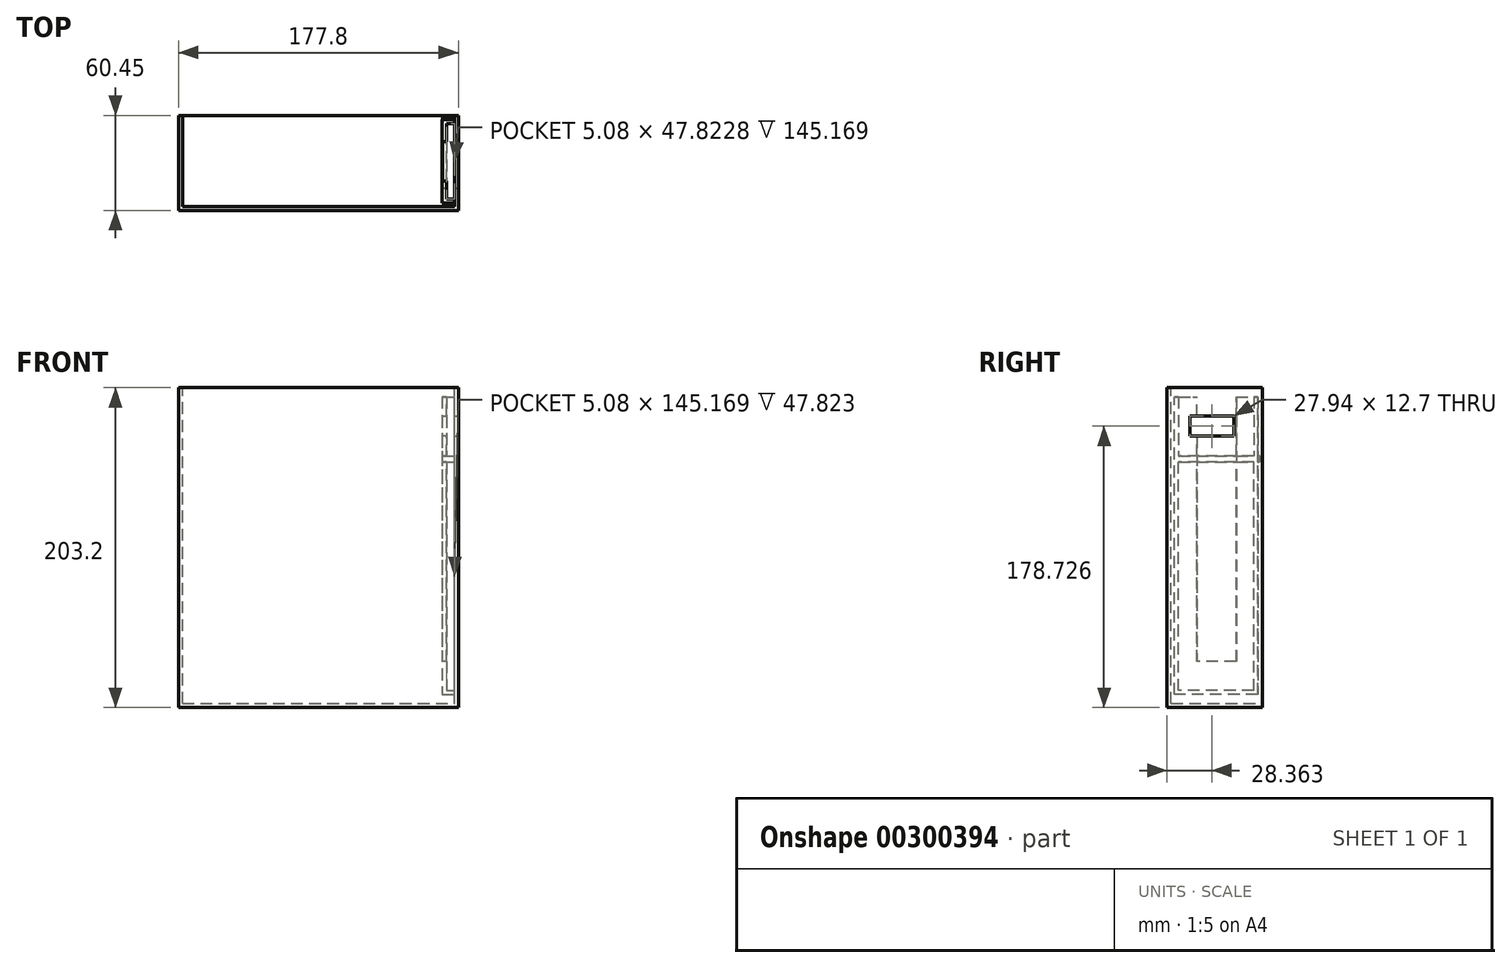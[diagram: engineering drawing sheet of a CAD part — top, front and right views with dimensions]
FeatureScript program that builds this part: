
annotation { "Feature Type Name" : "Feature", "Feature Type Description" : "" }
export const myFeature = defineFeature(function(context is Context, id is Id, definition is map)
    precondition{}
    {
        {
            var Q0;
            Q0=qCreatedBy(makeId("Front.planeOp"),FACE);
            var sketch = newSketch(context, id + "F0", { "sketchPlane" : qUnion([Q0])});
            skLineSegment(sketch, "E0.bottom", {"start": v(-89.23, 0) * mm, "end": v(88.57, 0) * mm});
            skLineSegment(sketch, "E0.top", {"start": v(-89.23, 203.2) * mm, "end": v(88.57, 203.2) * mm});
            skLineSegment(sketch, "E0.left", {"start": v(-89.23, 0) * mm, "end": v(-89.23, 203.2) * mm});
            skLineSegment(sketch, "E0.right", {"start": v(88.57, 0) * mm, "end": v(88.57, 203.2) * mm});
            skSolve(sketch);
        }
        {
            var Q0;
            Q0 = qSketchRegion(id + "F0", true);
            extrude(context, id + "F1", {"entities" : qUnion([Q0]), "depth" : 63.5 * mm});
        }
        {
            var Q0;
            Q0=makeQuery(id+"F1.opExtrude","SWEPT_FACE",FACE,{"disambiguationData":[OSD([sQuery(id+"F0.wireOp",EDGE,"E0.top")])]});
            shell(context, id + "F2", {"entities" : qUnion([Q0]), "thickness" : 2.54 * mm});
        }
        {
            var Q0;
            Q0=makeQuery(id+"F1.opExtrude","SWEPT_FACE",FACE,{"disambiguationData":[OSD([sQuery(id+"F0.wireOp",EDGE,"E0.right")])]});
            var sketch = newSketch(context, id + "F3", { "sketchPlane" : qUnion([Q0])});
            skLineSegment(sketch, "E1.bottom", {"start": v(-58.78, 197.36) * mm, "end": v(-5.88, 197.36) * mm});
            skLineSegment(sketch, "E1.top", {"start": v(-58.78, 8.2) * mm, "end": v(-5.88, 8.2) * mm});
            skLineSegment(sketch, "E1.left", {"start": v(-58.78, 197.36) * mm, "end": v(-58.78, 8.2) * mm});
            skLineSegment(sketch, "E1.right", {"start": v(-5.88, 197.36) * mm, "end": v(-5.88, 8.2) * mm});
            skSolve(sketch);
        }
        {
            var Q0;
            Q0 = qSketchRegion(id + "F3", true);
            extrude(context, id + "F4", {"entities" : qUnion([Q0]), "operationType" : NewBodyOperationType.ADD, "oppositeDirection" : true, "depth" : 10.16 * mm});
        }
        {
            var Q0;
            Q0=makeQuery(id+"F4.opExtrude","SWEPT_FACE",FACE,{"disambiguationData":[OSD([sQuery(id+"F3.wireOp",EDGE,"E1.bottom")])]});
            shell(context, id + "F5", {"entities" : qUnion([Q0]), "thickness" : 2.54 * mm});
        }
        {
            var Q0;
            Q0=makeQuery(id+"F4.opExtrude","CAP_FACE",FACE,{"disambiguationData":[OSD([sQuery(id+"F3.wireOp",EDGE,"E1.bottom"),sQuery(id+"F3.wireOp",EDGE,"E1.top"),sQuery(id+"F3.wireOp",EDGE,"E1.left"),sQuery(id+"F3.wireOp",EDGE,"E1.right")])],"isStart":false});
            var sketch = newSketch(context, id + "F6", { "sketchPlane" : qUnion([Q0])});
            skLineSegment(sketch, "E2.bottom", {"start": v(44.67, 197.36) * mm, "end": v(19.62, 197.36) * mm});
            skLineSegment(sketch, "E2.top", {"start": v(44.67, 8.2) * mm, "end": v(19.62, 8.2) * mm});
            skLineSegment(sketch, "E2.left", {"start": v(44.67, 197.36) * mm, "end": v(44.67, 8.2) * mm});
            skLineSegment(sketch, "E2.right", {"start": v(19.62, 197.36) * mm, "end": v(19.62, 8.2) * mm});
            skLineSegment(sketch, "E3", {"start": v(44.67, 29.18) * mm, "end": v(19.62, 29.18) * mm});
            skSolve(sketch);
        }
        {
            var Q0;
            {var subQ0=sQuery(id+"F6.wireOp",EDGE,"E2.bottom");Q0=makeQuery(id+"F6.imprint","IMPRINT",FACE,{"disambiguationData":[TD([[makeQuery(id+"F6.imprint","IMPRINT",EDGE,{"derivedFrom":subQ0}),1.0]])]});}
            extrude(context, id + "F7", {"entities" : qUnion([Q0]), "operationType" : NewBodyOperationType.REMOVE, "oppositeDirection" : true, "depth" : 5.84 * mm});
        }
        {
            var Q0;
            Q0=makeQuery(id+"F1.opExtrude","SWEPT_FACE",FACE,{"disambiguationData":[OSD([sQuery(id+"F0.wireOp",EDGE,"E0.right")])]});
            var sketch = newSketch(context, id + "F8", { "sketchPlane" : qUnion([Q0])});
            skLineSegment(sketch, "E4.bottom", {"start": v(-49.1, 190.16) * mm, "end": v(-21.17, 190.16) * mm});
            skLineSegment(sketch, "E4.top", {"start": v(-49.1, 159.68) * mm, "end": v(-21.17, 159.68) * mm});
            skLineSegment(sketch, "E4.left", {"start": v(-49.1, 190.16) * mm, "end": v(-49.1, 159.68) * mm});
            skLineSegment(sketch, "E4.right", {"start": v(-21.17, 190.16) * mm, "end": v(-21.17, 159.68) * mm});
            skLineSegment(sketch, "E5", {"start": v(-49.1, 172.38) * mm, "end": v(-21.17, 172.38) * mm});
            skLineSegment(sketch, "E6", {"start": v(-21.17, 185.08) * mm, "end": v(-49.1, 185.08) * mm});
            skSolve(sketch);
        }
        {
            var Q0;
            {var subQ0=sQuery(id+"F8.wireOp",EDGE,"E5");Q0=makeQuery(id+"F8.imprint","IMPRINT",FACE,{"disambiguationData":[TD([[makeQuery(id+"F8.imprint","IMPRINT",EDGE,{"derivedFrom":subQ0}),1.0]])]});}
            extrude(context, id + "F9", {"entities" : qUnion([Q0]), "operationType" : NewBodyOperationType.REMOVE, "oppositeDirection" : true, "depth" : 25.4 * mm});
        }
        {
            var Q0;
            Q0=makeQuery(id+"F1.opExtrude","SWEPT_FACE",FACE,{"disambiguationData":[OSD([sQuery(id+"F0.wireOp",EDGE,"E0.right")])]});
            var sketch = newSketch(context, id + "F10", { "sketchPlane" : qUnion([Q0])});
            skLineSegment(sketch, "E7.bottom", {"start": v(-58.79, 159.68) * mm, "end": v(-4.56, 159.68) * mm});
            skLineSegment(sketch, "E7.top", {"start": v(-58.79, 155.9) * mm, "end": v(-4.56, 155.9) * mm});
            skLineSegment(sketch, "E7.left", {"start": v(-58.79, 159.68) * mm, "end": v(-58.79, 155.9) * mm});
            skLineSegment(sketch, "E7.right", {"start": v(-4.56, 159.68) * mm, "end": v(-4.56, 155.9) * mm});
            skSolve(sketch);
        }
        {
            var Q0;
            Q0 = qSketchRegion(id + "F10", true);
            extrude(context, id + "F11", {"entities" : qUnion([Q0]), "operationType" : NewBodyOperationType.ADD, "oppositeDirection" : true, "depth" : 9.9 * mm});
        }
        {
            var Q0;
            Q0=makeQuery(id+"F1.opExtrude","CAP_FACE",FACE,{"disambiguationData":[OSD([sQuery(id+"F0.wireOp",EDGE,"E0.bottom"),sQuery(id+"F0.wireOp",EDGE,"E0.top"),sQuery(id+"F0.wireOp",EDGE,"E0.left"),sQuery(id+"F0.wireOp",EDGE,"E0.right")])],"isStart":true});
            extrude(context, id + "F12", {"entities" : qUnion([Q0]), "operationType" : NewBodyOperationType.REMOVE, "oppositeDirection" : true, "depth" : 3.05 * mm});
        }
    });
